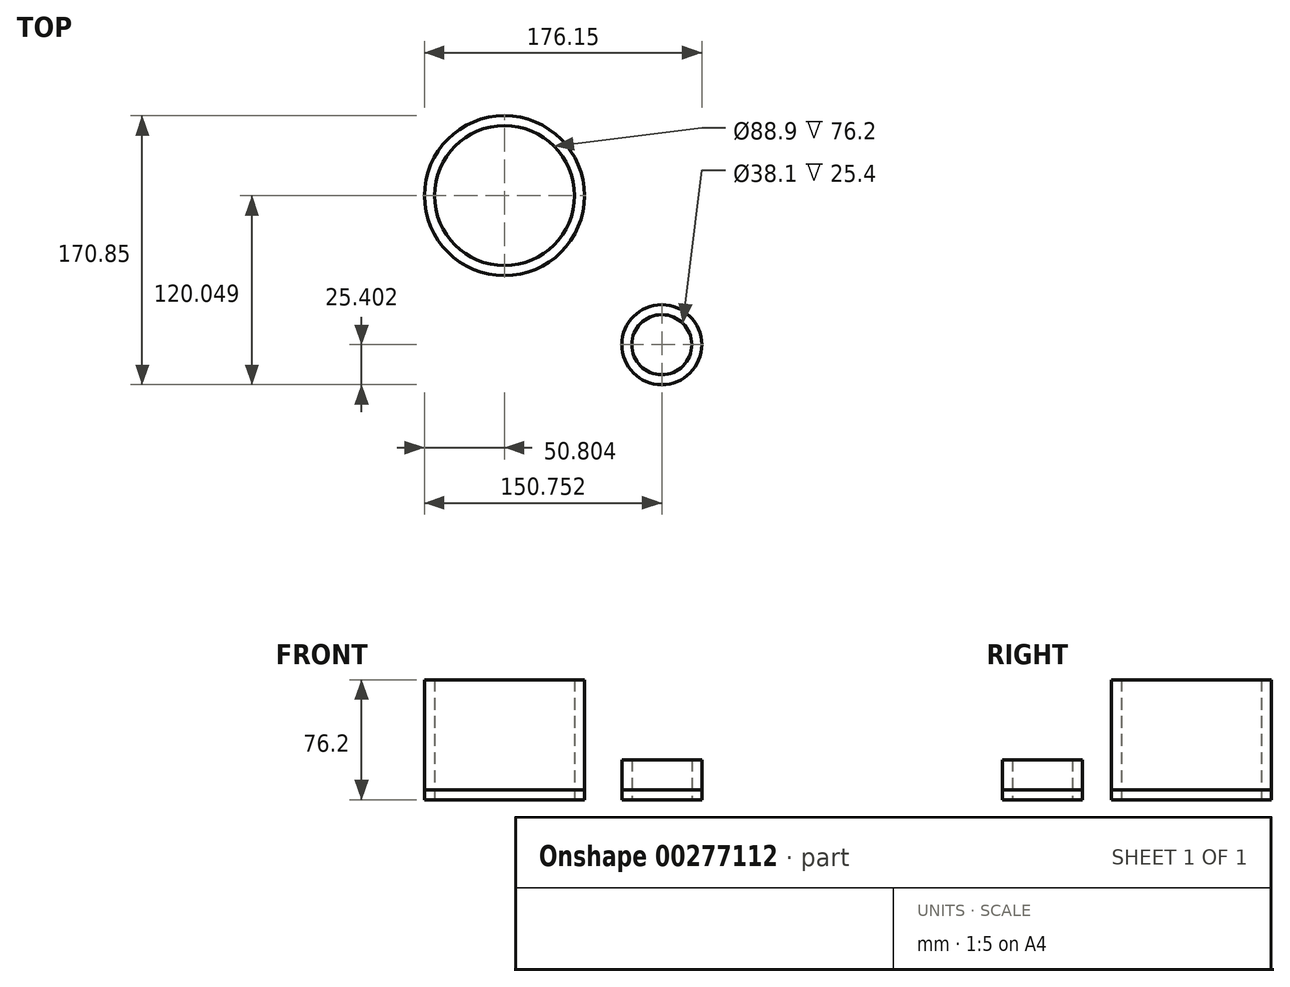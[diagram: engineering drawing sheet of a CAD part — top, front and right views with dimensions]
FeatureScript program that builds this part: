
annotation { "Feature Type Name" : "Feature", "Feature Type Description" : "" }
export const myFeature = defineFeature(function(context is Context, id is Id, definition is map)
    precondition{}
    {
        {
            var Q0;
            Q0=qCreatedBy(makeId("Top.planeOp"),FACE);
            var sketch = newSketch(context, id + "F0", { "sketchPlane" : qUnion([Q0])});
            skCircle(sketch, "E0", {"center": v(-46.13, 44.45) * mm, "radius": 50.8 * mm});
            skCircle(sketch, "E1", {"center": v(53.82, -50.2) * mm, "radius": 25.4 * mm});
            skCircle(sketch, "E2", {"center": v(-46.13, 44.45) * mm, "radius": 44.45 * mm});
            skCircle(sketch, "E3", {"center": v(53.82, -50.2) * mm, "radius": 19.05 * mm});
            skSolve(sketch);
        }
        {
            var Q0;
            Q0 = qSketchRegion(id + "F0", true);
            var Q1;
            Q1=makeQuery(id+"F0.imprint","IMPRINT",FACE,{"disambiguationData":[TD([[makeQuery(id+"F0.imprint","IMPRINT",EDGE,{"derivedFrom":sQuery(id+"F0.wireOp",EDGE,"E2")}),1.0]])]});
            var Q2;
            Q2=makeQuery(id+"F0.imprint","IMPRINT",FACE,{"disambiguationData":[TD([[makeQuery(id+"F0.imprint","IMPRINT",EDGE,{"derivedFrom":sQuery(id+"F0.wireOp",EDGE,"E3")}),1.0]])]});
            extrude(context, id + "F1", {"entities" : qUnion([Q0, Q1, Q2]), "depth" : 6.35 * mm});
        }
        {
            var Q0;
            Q0=makeQuery(id+"F0.imprint","IMPRINT",FACE,{"disambiguationData":[TD([[makeQuery(id+"F0.imprint","IMPRINT",EDGE,{"derivedFrom":sQuery(id+"F0.wireOp",EDGE,"E0")}),1.0]])]});
            extrude(context, id + "F2", {"entities" : qUnion([Q0]), "depth" : 76.2 * mm});
        }
        {
            var Q0;
            Q0=makeQuery(id+"F0.imprint","IMPRINT",FACE,{"disambiguationData":[TD([[makeQuery(id+"F0.imprint","IMPRINT",EDGE,{"derivedFrom":sQuery(id+"F0.wireOp",EDGE,"E1")}),1.0]])]});
            extrude(context, id + "F3", {"entities" : qUnion([Q0]), "depth" : 25.4 * mm});
        }
    });
